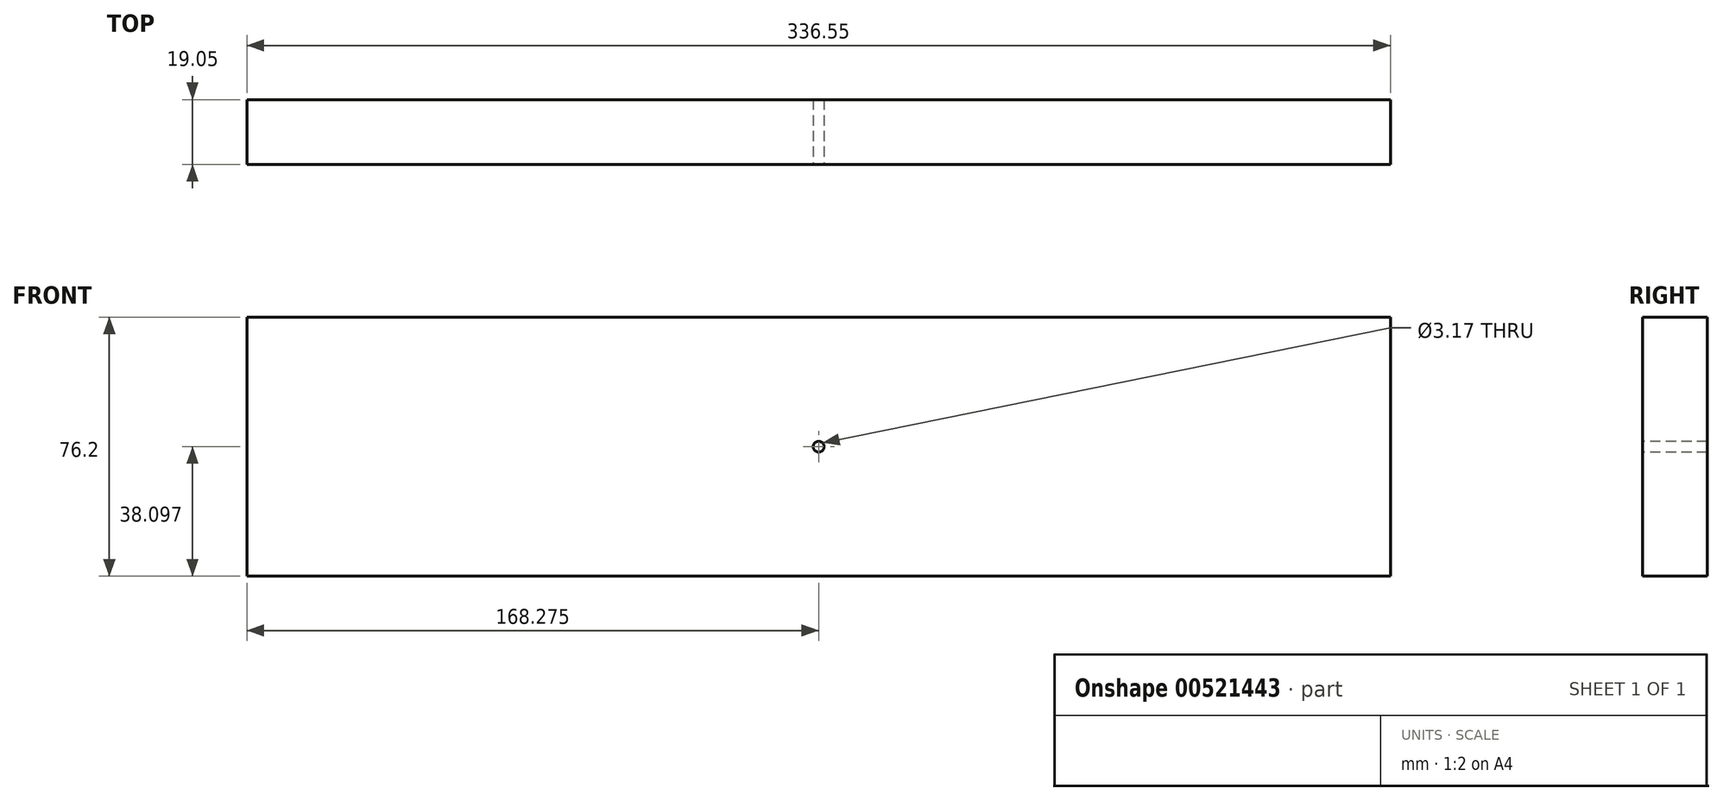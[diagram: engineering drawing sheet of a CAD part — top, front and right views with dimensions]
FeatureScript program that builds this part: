
annotation { "Feature Type Name" : "Feature", "Feature Type Description" : "" }
export const myFeature = defineFeature(function(context is Context, id is Id, definition is map)
    precondition{}
    {
        {
            var Q0;
            Q0=qCreatedBy(makeId("Front.planeOp"),FACE);
            var sketch = newSketch(context, id + "F0", { "sketchPlane" : qUnion([Q0])});
            skLineSegment(sketch, "E0.bottom", {"start": v(-67.77, 40.63) * mm, "end": v(268.78, 40.63) * mm});
            skLineSegment(sketch, "E0.top", {"start": v(-67.77, -35.57) * mm, "end": v(268.78, -35.57) * mm});
            skLineSegment(sketch, "E0.left", {"start": v(-67.77, 40.63) * mm, "end": v(-67.77, -35.57) * mm});
            skLineSegment(sketch, "E0.right", {"start": v(268.78, 40.63) * mm, "end": v(268.78, -35.57) * mm});
            skSolve(sketch);
        }
        {
            var Q0;
            Q0=makeQuery(id+"F0.imprint","IMPRINT",FACE,{"disambiguationData":[TD([[makeQuery(id+"F0.imprint","IMPRINT",EDGE,{"derivedFrom":sQuery(id+"F0.wireOp",EDGE,"E0.bottom")}),-1.0]])]});
            extrude(context, id + "F1", {"entities" : qUnion([Q0]), "depth" : 19.05 * mm, "offsetDistance" : 25.4 * mm});
        }
        {
            var Q0;
            Q0=makeQuery(id+"F1.opExtrude","CAP_FACE",FACE,{"disambiguationData":[OSD([sQuery(id+"F0.wireOp",EDGE,"E0.bottom"),sQuery(id+"F0.wireOp",EDGE,"E0.top"),sQuery(id+"F0.wireOp",EDGE,"E0.left"),sQuery(id+"F0.wireOp",EDGE,"E0.right")])],"isStart":false});
            var sketch = newSketch(context, id + "F2", { "sketchPlane" : qUnion([Q0])});
            skLineSegment(sketch, "E1", {"start": v(100.5, 40.63) * mm, "end": v(100.5, -35.57) * mm});
            skPoint(sketch, "E2", {"position": v(100.5, 2.53) * mm});
            skSolve(sketch);
        }
        {
            var Q0;
            Q0=sQuery(id+"F2.wireOp",VERTEX,"E2");
            var Q1;
            Q1=makeQuery(id+"F1.opExtrude","SWEPT_BODY",BODY,{"disambiguationData":[OSD([sQuery(id+"F0.wireOp",EDGE,"E0.bottom"),sQuery(id+"F0.wireOp",EDGE,"E0.top"),sQuery(id+"F0.wireOp",EDGE,"E0.left"),sQuery(id+"F0.wireOp",EDGE,"E0.right")])]});
            hole(context, id + "F3", {"style" : HoleStyle.SIMPLE, "endStyle" : HoleEndStyle.THROUGH, "holeDiameter" : 3.17 * mm, "isTappedThrough" : true, "tappedDepth" : 12.7 * mm, "tapClearance" : 3, "locations" : qUnion([Q0]), "scope" : qUnion([Q1])});
        }
    });
